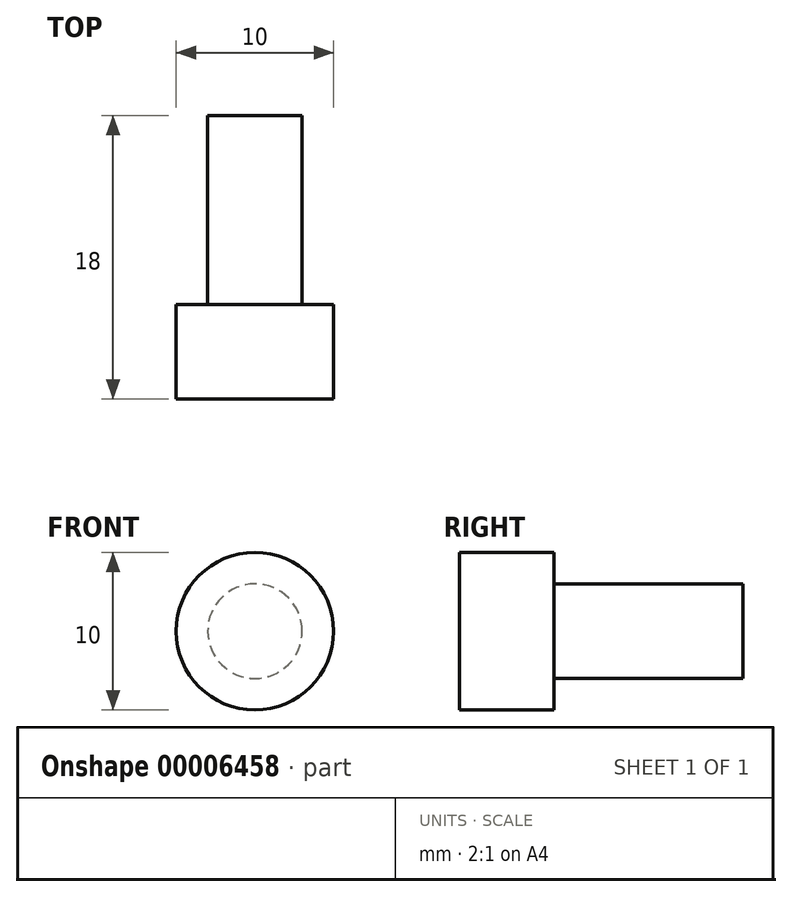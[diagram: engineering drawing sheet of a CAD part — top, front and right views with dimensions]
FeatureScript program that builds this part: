
annotation { "Feature Type Name" : "Feature", "Feature Type Description" : "" }
export const myFeature = defineFeature(function(context is Context, id is Id, definition is map)
    precondition{}
    {
        {
            var Q0;
            Q0=qCreatedBy(makeId("Right.planeOp"),FACE);
            var sketch = newSketch(context, id + "F0", { "sketchPlane" : qUnion([Q0])});
            skLineSegment(sketch, "E0", {"start": v(0, 0) * mm, "end": v(0, 5) * mm});
            skLineSegment(sketch, "E1", {"start": v(0, 5) * mm, "end": v(6, 5) * mm});
            skLineSegment(sketch, "E2", {"start": v(6, 5) * mm, "end": v(6, 3) * mm});
            skLineSegment(sketch, "E3", {"start": v(6, 3) * mm, "end": v(18, 3) * mm});
            skLineSegment(sketch, "E4", {"start": v(18, 3) * mm, "end": v(18, 0) * mm});
            skLineSegment(sketch, "E5", {"start": v(18, 0) * mm, "end": v(0, 0) * mm});
            skSolve(sketch);
        }
        {
            var Q0;
            Q0 = qSketchRegion(id + "F0", true);
            var Q1;
            Q1=sQuery(id+"F0.wireOp",EDGE,"E5");
            revolve(context, id + "F1", {"entities" : qUnion([Q0]), "axis" : qUnion([Q1]), "revolveType" : RevolveType.FULL});
        }
    });
